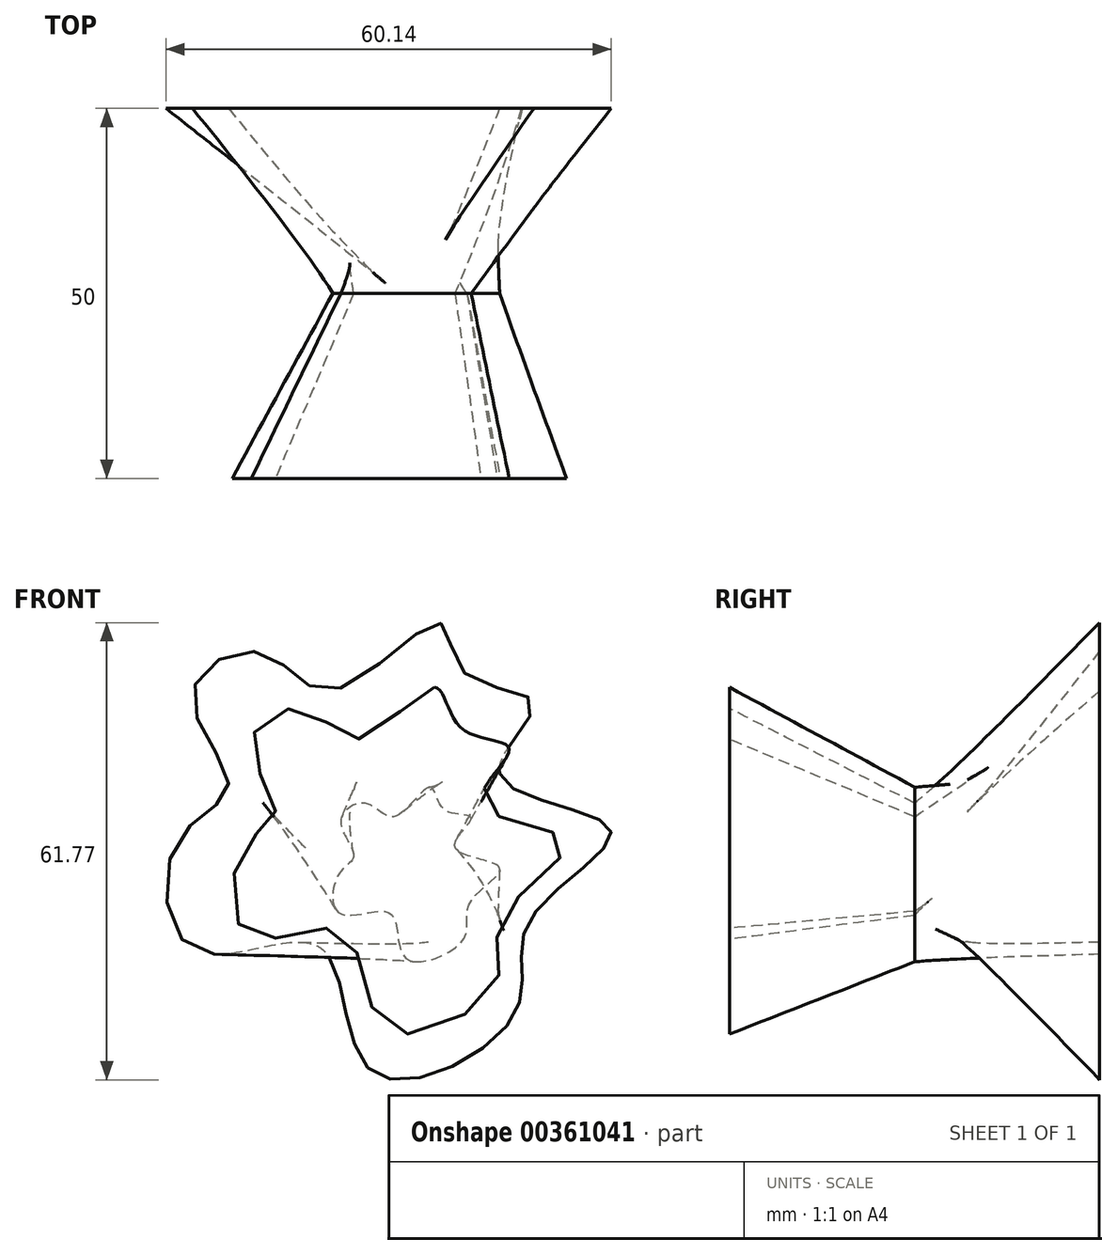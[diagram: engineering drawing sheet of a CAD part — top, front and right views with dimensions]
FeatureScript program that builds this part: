
annotation { "Feature Type Name" : "Feature", "Feature Type Description" : "" }
export const myFeature = defineFeature(function(context is Context, id is Id, definition is map)
    precondition{}
    {
        {
            var Q0;
            Q0=qCreatedBy(makeId("Front.planeOp"),FACE);
            var sketch = newSketch(context, id + "F0", { "sketchPlane" : qUnion([Q0])});
            skFitSpline(sketch, "E0", {"points": [v(0, 14.14) * mm, v(-4.78, 10.2) * mm, v(-8.63, 11.94) * mm, v(-12.03, 9.64) * mm, v(-10.29, 4.96) * mm, v(-12.3, 2.39) * mm, v(-12.12, -2.94) * mm, v(-5.33, -2.94) * mm, v(-3.21, -9) * mm, v(4.6, -6.34) * mm, v(5.34, -1.55) * mm, v(9.37, 3.27) * mm, v(3.4, 6.06) * mm, v(5.56, 9.97) * mm, v(2.03, 11.08) * mm, v(0, 14.14) * mm]});
            skLineSegment(sketch, "E1", {"start": v(-21.77, 14.14) * mm, "end": v(31.32, 14.14) * mm, "construction": true});
            skLineSegment(sketch, "E2", {"start": v(-22.68, -9.46) * mm, "end": v(33.34, -9.46) * mm, "construction": true});
            skLineSegment(sketch, "E3", {"start": v(-13.13, 25.99) * mm, "end": v(-13.13, -18.1) * mm, "construction": true});
            skLineSegment(sketch, "E4", {"start": v(9.37, 26.17) * mm, "end": v(9.37, -18.73) * mm, "construction": true});
            skSolve(sketch);
        }
        {
            var Q0;
            Q0=qCreatedBy(makeId("Front.planeOp"),FACE);
            cPlane(context, id + "F1", {"entities" : qUnion([Q0]), "cplaneType" : CPlaneType.OFFSET, "offset" : 25 * mm, "width" : 150 * mm, "height" : 150 * mm});
        }
        {
            var Q0;
            Q0=qCreatedBy(id+"F1.planeOp",FACE);
            var sketch = newSketch(context, id + "F2", { "sketchPlane" : qUnion([Q0])});
            skFitSpline(sketch, "E5", {"points": [v(0.6, 27.64) * mm, v(-9.45, 20.68) * mm, v(-17.02, 24.65) * mm, v(-24.1, 20.32) * mm, v(-20.88, 10.78) * mm, v(-25.27, 5.83) * mm, v(-24.26, -6.04) * mm, v(-11.71, -5.4) * mm, v(-5.7, -18.53) * mm, v(8.98, -12.28) * mm, v(9.62, -3.6) * mm, v(18.35, 6.82) * mm, v(6.98, 11.94) * mm, v(10.71, 19.27) * mm, v(4.34, 22.06) * mm, v(0.6, 27.64) * mm]});
            skLineSegment(sketch, "E6", {"start": v(-26.65, 48.15) * mm, "end": v(-26.65, -37.44) * mm, "construction": true});
            skLineSegment(sketch, "E7", {"start": v(18.35, 50.17) * mm, "end": v(18.35, -36.53) * mm, "construction": true});
            skLineSegment(sketch, "E8", {"start": v(-40.57, 27.64) * mm, "end": v(45.92, 27.64) * mm, "construction": true});
            skLineSegment(sketch, "E9", {"start": v(-39.65, -19.36) * mm, "end": v(49.24, -19.36) * mm, "construction": true});
            skSolve(sketch);
        }
        {
            var Q0;
            Q0=makeQuery(id+"F2.imprint","IMPRINT",FACE,{"disambiguationData":[TD([[makeQuery(id+"F2.imprint","IMPRINT",EDGE,{"derivedFrom":sQuery(id+"F2.wireOp",EDGE,"E5")}),1.0]])]});
            var Q1;
            Q1=makeQuery(id+"F0.imprint","IMPRINT",FACE,{"disambiguationData":[TD([[makeQuery(id+"F0.imprint","IMPRINT",EDGE,{"derivedFrom":sQuery(id+"F0.wireOp",EDGE,"E0")}),1.0]])]});
            loft(context, id + "F3", {"sheetProfilesArray" : [{ "sheetProfileEntities" : qUnion([Q0]) }, { "sheetProfileEntities" : qUnion([Q1]) }]});
        }
        {
            var Q0;
            Q0=qCreatedBy(makeId("Front.planeOp"),FACE);
            cPlane(context, id + "F4", {"entities" : qUnion([Q0]), "cplaneType" : CPlaneType.OFFSET, "offset" : 25 * mm, "oppositeDirection" : true, "width" : 150 * mm, "height" : 150 * mm});
        }
        {
            var Q0;
            Q0=qCreatedBy(id+"F4.planeOp",FACE);
            var sketch = newSketch(context, id + "F5", { "sketchPlane" : qUnion([Q0])});
            skFitSpline(sketch, "E10", {"points": [v(1.26, 36.35) * mm, v(-13.34, 27.21) * mm, v(-22.81, 32.34) * mm, v(-32.05, 26.75) * mm, v(-27.2, 14.35) * mm, v(-34.12, 6.8) * mm, v(-31.69, -7.9) * mm, v(-14.8, -7.56) * mm, v(-7.62, -24.44) * mm, v(11.46, -16.56) * mm, v(13.43, -3.9) * mm, v(24.36, 8.51) * mm, v(9.53, 15.68) * mm, v(14.03, 25.41) * mm, v(4.67, 29.54) * mm, v(1.26, 36.35) * mm]});
            skPoint(sketch, "E11", {"position": v(-35.64, 0) * mm});
            skLineSegment(sketch, "E12", {"start": v(24.36, 47.66) * mm, "end": v(24.36, -35.26) * mm, "construction": true});
            skLineSegment(sketch, "E13", {"start": v(-35.64, 48.15) * mm, "end": v(-35.64, -36.35) * mm, "construction": true});
            skSolve(sketch);
        }
        {
            var Q1;
            Q1=makeQuery(id+"F3.opLoft","CAP_FACE",FACE,{"disambiguationData":[OSD([makeQuery(id+"F0.imprint","IMPRINT",FACE,{"disambiguationData":[TD([[makeQuery(id+"F0.imprint","IMPRINT",EDGE,{"derivedFrom":sQuery(id+"F0.wireOp",EDGE,"E0")}),1.0]])]})])],"isStart":true});
            var Q2;
            Q2=makeQuery(id+"F5.imprint","IMPRINT",FACE,{"disambiguationData":[TD([[makeQuery(id+"F5.imprint","IMPRINT",EDGE,{"derivedFrom":sQuery(id+"F5.wireOp",EDGE,"E10")}),1.0]])]});
            loft(context, id + "F6", {"operationType" : NewBodyOperationType.ADD, "sheetProfilesArray" : [{ "sheetProfileEntities" : qUnion([Q1]) }, { "sheetProfileEntities" : qUnion([Q2]) }]});
        }
    });
